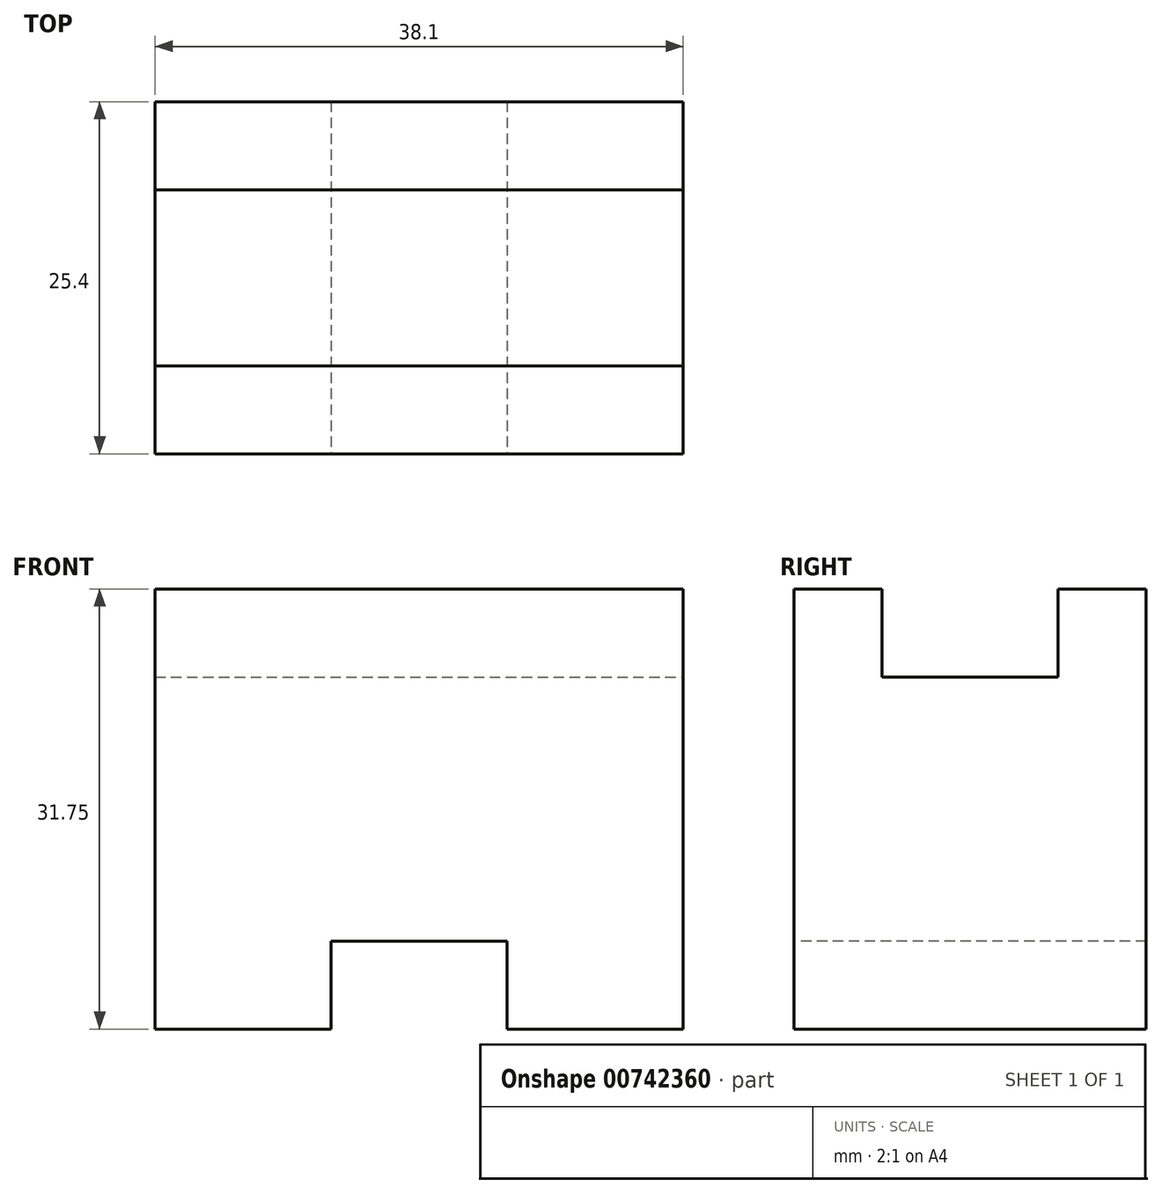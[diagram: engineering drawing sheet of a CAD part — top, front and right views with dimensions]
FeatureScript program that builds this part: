
annotation { "Feature Type Name" : "Feature", "Feature Type Description" : "" }
export const myFeature = defineFeature(function(context is Context, id is Id, definition is map)
    precondition{}
    {
        {
            var Q0;
            Q0=qCreatedBy(makeId("Front.planeOp"),FACE);
            var sketch = newSketch(context, id + "F0", { "sketchPlane" : qUnion([Q0])});
            skLineSegment(sketch, "E0", {"start": v(0, 31.75) * mm, "end": v(0, 0) * mm});
            skLineSegment(sketch, "E1", {"start": v(0, 0) * mm, "end": v(38.1, 0) * mm});
            skLineSegment(sketch, "E2", {"start": v(38.1, 31.75) * mm, "end": v(0, 31.75) * mm});
            skLineSegment(sketch, "E3", {"start": v(38.1, 31.75) * mm, "end": v(38.1, 0) * mm});
            skSolve(sketch);
        }
        {
            var Q0;
            Q0=makeQuery(id+"F0.imprint","IMPRINT",FACE,{"disambiguationData":[TD([[makeQuery(id+"F0.imprint","IMPRINT",EDGE,{"derivedFrom":sQuery(id+"F0.wireOp",EDGE,"E0")}),1.0]])]});
            extrude(context, id + "F1", {"entities" : qUnion([Q0]), "depth" : 25.4 * mm, "offsetDistance" : 25.4 * mm});
        }
        {
            var Q0;
            Q0=makeQuery(id+"F1.opExtrude","CAP_FACE",FACE,{"disambiguationData":[OSD([sQuery(id+"F0.wireOp",EDGE,"E0"),sQuery(id+"F0.wireOp",EDGE,"E1"),sQuery(id+"F0.wireOp",EDGE,"E2"),sQuery(id+"F0.wireOp",EDGE,"E3")])],"isStart":false});
            var sketch = newSketch(context, id + "F2", { "sketchPlane" : qUnion([Q0])});
            skLineSegment(sketch, "E4", {"start": v(12.7, 0) * mm, "end": v(12.7, 6.35) * mm});
            skLineSegment(sketch, "E5", {"start": v(12.7, 6.35) * mm, "end": v(25.4, 6.35) * mm});
            skLineSegment(sketch, "E6", {"start": v(25.4, 6.35) * mm, "end": v(25.4, 0) * mm});
            skLineSegment(sketch, "E7", {"start": v(25.4, 0) * mm, "end": v(12.7, 0) * mm});
            skSolve(sketch);
        }
        {
            var Q0;
            Q0 = qSketchRegion(id + "F2", true);
            extrude(context, id + "F3", {"entities" : qUnion([Q0]), "operationType" : NewBodyOperationType.REMOVE, "endBound" : BoundingType.THROUGH_ALL, "oppositeDirection" : true, "depth" : 25.4 * mm, "offsetDistance" : 25.4 * mm});
        }
        {
            var Q0;
            Q0=makeQuery(id+"F1.opExtrude","SWEPT_FACE",FACE,{"disambiguationData":[OSD([sQuery(id+"F0.wireOp",EDGE,"E3")])]});
            var sketch = newSketch(context, id + "F4", { "sketchPlane" : qUnion([Q0])});
            skLineSegment(sketch, "E8", {"start": v(-19.05, 31.75) * mm, "end": v(-19.05, 25.4) * mm});
            skLineSegment(sketch, "E9", {"start": v(-19.05, 25.4) * mm, "end": v(-6.35, 25.4) * mm});
            skLineSegment(sketch, "E10", {"start": v(-6.35, 25.4) * mm, "end": v(-6.35, 31.75) * mm});
            skLineSegment(sketch, "E11", {"start": v(-19.05, 31.75) * mm, "end": v(-6.35, 31.75) * mm});
            skSolve(sketch);
        }
        {
            var Q0;
            Q0 = qSketchRegion(id + "F4", true);
            extrude(context, id + "F5", {"entities" : qUnion([Q0]), "operationType" : NewBodyOperationType.REMOVE, "endBound" : BoundingType.THROUGH_ALL, "oppositeDirection" : true, "depth" : 25.4 * mm, "offsetDistance" : 25.4 * mm});
        }
    });
